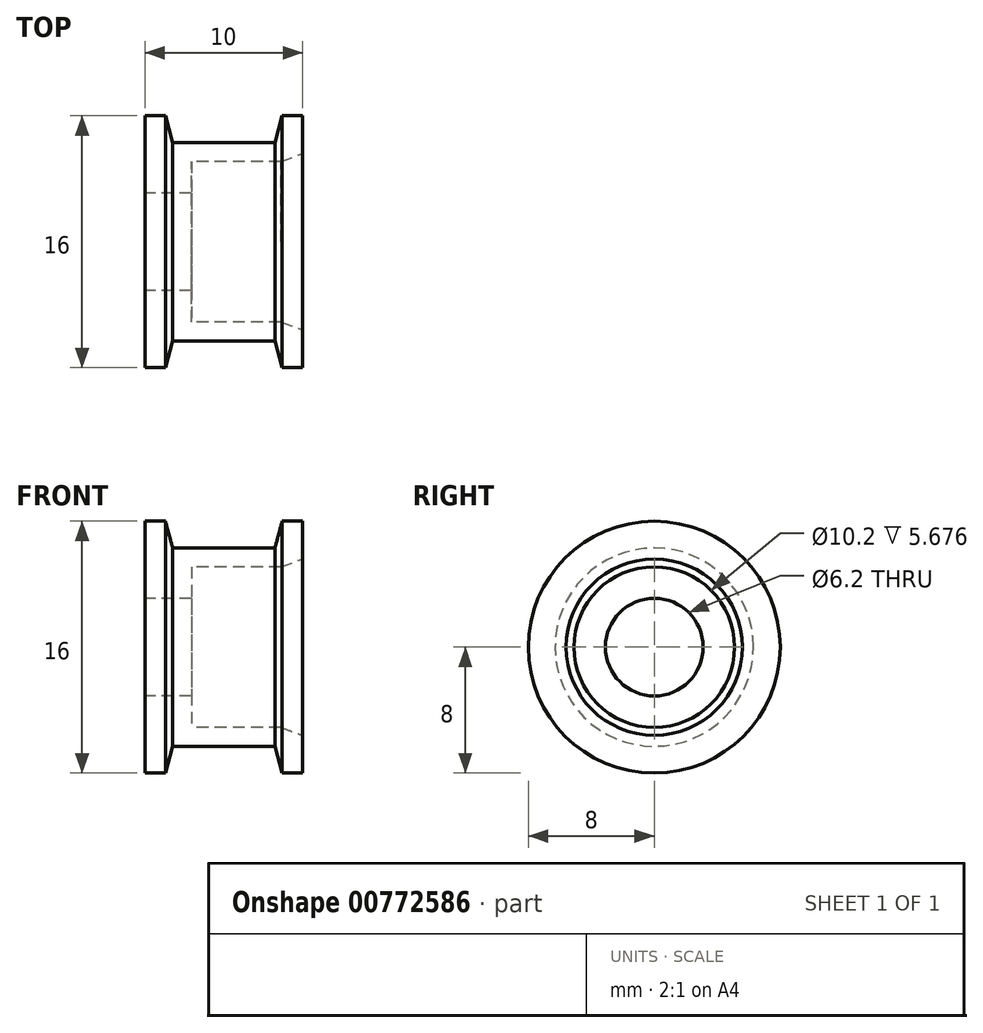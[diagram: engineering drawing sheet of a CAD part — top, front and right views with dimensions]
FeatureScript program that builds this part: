
annotation { "Feature Type Name" : "Feature", "Feature Type Description" : "" }
export const myFeature = defineFeature(function(context is Context, id is Id, definition is map)
    precondition{}
    {
        {
            var Q0;
            Q0=qCreatedBy(makeId("Front.planeOp"),FACE);
            var sketch = newSketch(context, id + "F0", { "sketchPlane" : qUnion([Q0])});
            skLineSegment(sketch, "E0", {"start": v(-2.05, 0) * mm, "end": v(2.05, 0) * mm, "construction": true});
            skLineSegment(sketch, "E1.rect.bottom", {"start": v(1.25, 5.1) * mm, "end": v(-1.25, 5.1) * mm});
            skLineSegment(sketch, "E1.rect.top", {"start": v(1.25, -5.1) * mm, "end": v(-1.25, -5.1) * mm});
            skLineSegment(sketch, "E1.rect.left", {"start": v(2.05, 4.3) * mm, "end": v(2.05, -4.3) * mm});
            skLineSegment(sketch, "E1.rect.right", {"start": v(-2.05, 5.1) * mm, "end": v(-2.05, -4.3) * mm});
            skPoint(sketch, "E1.rect.middle", {"position": v(0, 0) * mm});
            skLineSegment(sketch, "E2", {"start": v(0, 0) * mm, "end": v(0, 8) * mm, "construction": true});
            skLineSegment(sketch, "E3", {"start": v(-5, 8) * mm, "end": v(-3.7, 8) * mm});
            skLineSegment(sketch, "E4", {"start": v(-3.7, 8) * mm, "end": v(-3.25, 6.3) * mm});
            skLineSegment(sketch, "E5", {"start": v(-5, 8) * mm, "end": v(-5, 3.1) * mm});
            skLineSegment(sketch, "E6", {"start": v(-5, 3.1) * mm, "end": v(-2.05, 3.1) * mm});
            skLineSegment(sketch, "E7.0.MirrorCS", {"start": v(3.7, 8) * mm, "end": v(3.25, 6.3) * mm});
            skLineSegment(sketch, "E8.0.MirrorCS", {"start": v(5, 8) * mm, "end": v(3.7, 8) * mm});
            skLineSegment(sketch, "E9.0.MirrorCS", {"start": v(5, 8) * mm, "end": v(5, 5.1) * mm});
            skLineSegment(sketch, "E10", {"start": v(-3.25, 6.3) * mm, "end": v(3.25, 6.3) * mm});
            skLineSegment(sketch, "E11", {"start": v(-2.05, 5.1) * mm, "end": v(5, 5.1) * mm});
            skPoint(sketch, "E12.visualSharp", {"position": v(2.05, 5.1) * mm});
            skArc(sketch, "E12.filletArc", {"start": v(2.05, 4.3) * mm, "mid": v(1.82, 4.87) * mm, "end": v(1.25, 5.1) * mm});
            skPoint(sketch, "E13.visualSharp", {"position": v(-2.05, 5.1) * mm});
            skArc(sketch, "E13.filletArc", {"start": v(-1.25, 5.1) * mm, "mid": v(-1.82, 4.87) * mm, "end": v(-2.05, 4.3) * mm});
            skPoint(sketch, "E14.visualSharp", {"position": v(2.05, -5.1) * mm});
            skArc(sketch, "E14.filletArc", {"start": v(1.25, -5.1) * mm, "mid": v(1.82, -4.87) * mm, "end": v(2.05, -4.3) * mm});
            skPoint(sketch, "E15.visualSharp", {"position": v(-2.05, -5.1) * mm});
            skArc(sketch, "E15.filletArc", {"start": v(-2.05, -4.3) * mm, "mid": v(-1.82, -4.87) * mm, "end": v(-1.25, -5.1) * mm});
            skSolve(sketch);
        }
        {
            var Q0;
            {var subQ2=sQuery(id+"F0.wireOp",EDGE,"E1.rect.bottom");Q0=makeQuery(id+"F0.imprint","IMPRINT",FACE,{"disambiguationData":[TD([[makeQuery(id+"F0.imprint","IMPRINT",EDGE,{"derivedFrom":subQ2}),-1.0]])]});}
            var Q1;
            Q1=sQuery(id+"F0.wireOp",EDGE,"E0");
            revolve(context, id + "F1", {"entities" : qUnion([Q0]), "axis" : qUnion([Q1]), "revolveType" : RevolveType.FULL});
        }
        {
            var Q0;
            Q0=makeQuery(id+"F1.opRevolve","SWEPT_EDGE",EDGE,{"disambiguationData":[OSD([sQuery(id+"F0.wireOp",EDGE,"E9.0.MirrorCS"),sQuery(id+"F0.wireOp",EDGE,"E11")])]});
            chamfer(context, id + "F2", {"entities" : qUnion([Q0]), "chamferType" : ChamferType.OFFSET_ANGLE, "width" : 0.5 * mm, "oppositeDirection" : false, "angle" : 70 * degree, "tangentPropagation" : true});
        }
    });
